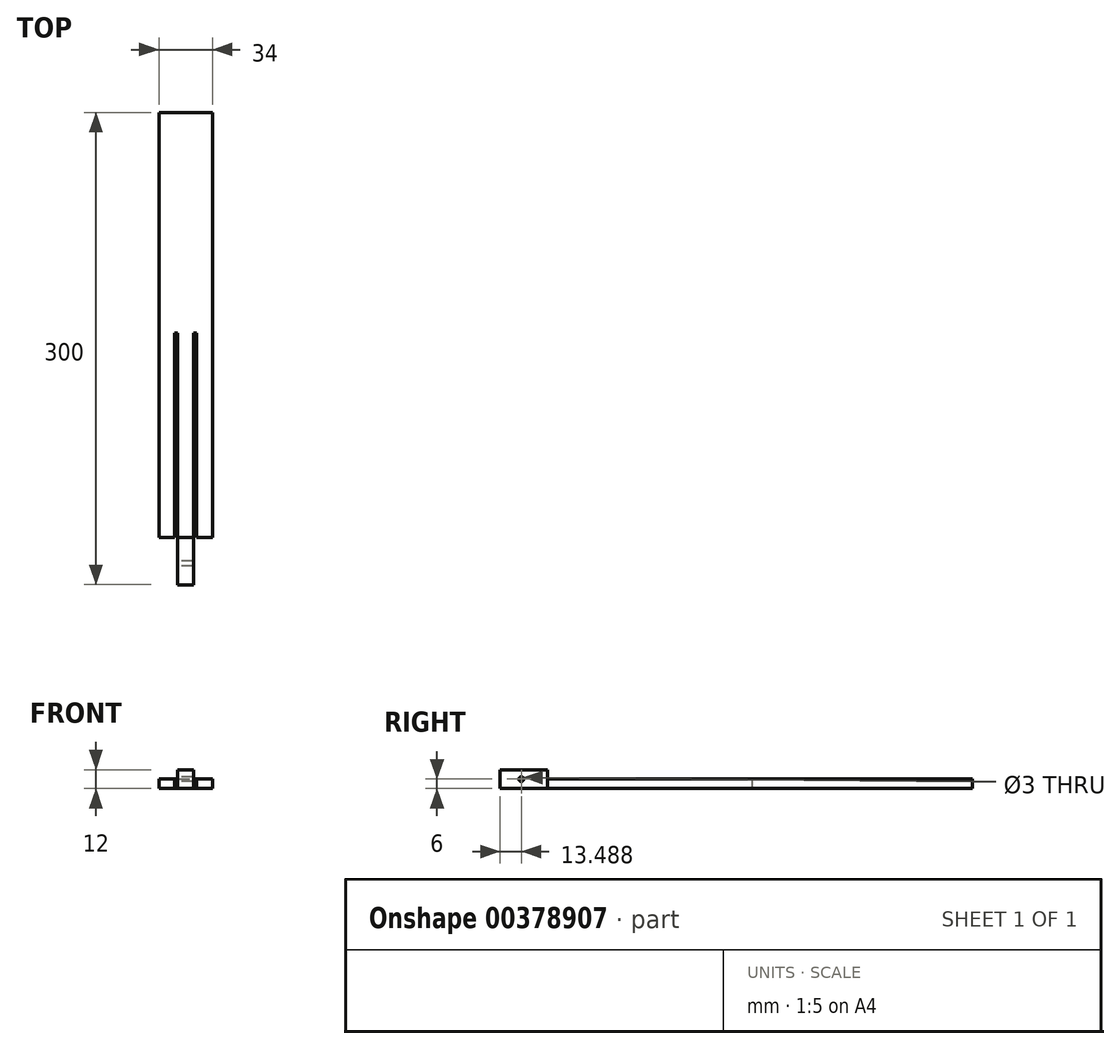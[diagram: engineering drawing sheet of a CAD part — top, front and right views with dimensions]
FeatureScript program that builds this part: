
annotation { "Feature Type Name" : "Feature", "Feature Type Description" : "" }
export const myFeature = defineFeature(function(context is Context, id is Id, definition is map)
    precondition{}
    {
        {
            var Q0;
            Q0=qCreatedBy(makeId("Top.planeOp"),FACE);
            var sketch = newSketch(context, id + "F0", { "sketchPlane" : qUnion([Q0])});
            skLineSegment(sketch, "E0.bottom", {"start": v(-19.09, 227.5) * mm, "end": v(14.91, 227.5) * mm});
            skLineSegment(sketch, "E0.left", {"start": v(-19.09, 227.5) * mm, "end": v(-19.09, -42.5) * mm});
            skLineSegment(sketch, "E0.right", {"start": v(14.91, 227.5) * mm, "end": v(14.91, -42.5) * mm});
            skLineSegment(sketch, "E1.top", {"start": v(-9.09, 87.5) * mm, "end": v(-7.09, 87.5) * mm});
            skLineSegment(sketch, "E1.left", {"start": v(-9.09, -42.5) * mm, "end": v(-9.09, 87.5) * mm});
            skLineSegment(sketch, "E1.right", {"start": v(-7.09, -72.5) * mm, "end": v(-7.09, 87.5) * mm});
            skLineSegment(sketch, "E2.top", {"start": v(2.91, 87.5) * mm, "end": v(4.91, 87.5) * mm});
            skLineSegment(sketch, "E2.left", {"start": v(2.91, -72.5) * mm, "end": v(2.91, 87.5) * mm});
            skLineSegment(sketch, "E2.right", {"start": v(4.91, -42.5) * mm, "end": v(4.91, 87.5) * mm});
            skLineSegment(sketch, "E3.trimOffspring", {"start": v(-7.09, -72.5) * mm, "end": v(2.91, -72.5) * mm});
            skLineSegment(sketch, "E4.top", {"start": v(-19.09, -42.5) * mm, "end": v(-9.09, -42.5) * mm});
            skLineSegment(sketch, "E5.top", {"start": v(4.91, -42.5) * mm, "end": v(14.91, -42.5) * mm});
            skSolve(sketch);
        }
        {
            var Q0;
            Q0=makeQuery(id+"F0.imprint","IMPRINT",FACE,{"disambiguationData":[TD([[makeQuery(id+"F0.imprint","IMPRINT",EDGE,{"derivedFrom":sQuery(id+"F0.wireOp",EDGE,"E0.bottom")}),-1.0]])]});
            extrude(context, id + "F1", {"entities" : qUnion([Q0]), "depth" : 6 * mm});
        }
        {
            var Q0;
            Q0=makeQuery(id+"F1.opExtrude","CAP_FACE",FACE,{"disambiguationData":[OSD([sQuery(id+"F0.wireOp",EDGE,"E0.bottom"),sQuery(id+"F0.wireOp",EDGE,"E0.left"),sQuery(id+"F0.wireOp",EDGE,"E0.right"),sQuery(id+"F0.wireOp",EDGE,"E1.top"),sQuery(id+"F0.wireOp",EDGE,"E1.left"),sQuery(id+"F0.wireOp",EDGE,"E1.right"),sQuery(id+"F0.wireOp",EDGE,"E2.top"),sQuery(id+"F0.wireOp",EDGE,"E2.left"),sQuery(id+"F0.wireOp",EDGE,"E2.right"),sQuery(id+"F0.wireOp",EDGE,"E3.trimOffspring"),sQuery(id+"F0.wireOp",EDGE,"E4.top"),sQuery(id+"F0.wireOp",EDGE,"E5.top")])],"isStart":false});
            var sketch = newSketch(context, id + "F2", { "sketchPlane" : qUnion([Q0])});
            skLineSegment(sketch, "E6.bottom", {"start": v(-7.09, -42.5) * mm, "end": v(2.91, -42.5) * mm});
            skLineSegment(sketch, "E6.top", {"start": v(-7.09, -72.5) * mm, "end": v(2.91, -72.5) * mm});
            skLineSegment(sketch, "E6.left", {"start": v(-7.09, -42.5) * mm, "end": v(-7.09, -72.5) * mm});
            skLineSegment(sketch, "E6.right", {"start": v(2.91, -42.5) * mm, "end": v(2.91, -72.5) * mm});
            skSolve(sketch);
        }
        {
            var Q0;
            Q0=qSketchRegion(id+"F2",true);
            extrude(context, id + "F3", {"entities" : qUnion([Q0]), "operationType" : NewBodyOperationType.ADD, "depth" : 6 * mm});
        }
        {
            var Q0;
            Q0=makeQuery(id+"F3.boolean.opBoolean","MERGE",FACE,{"derivedFrom":[makeQuery(id+"F1.opExtrude","SWEPT_FACE",FACE,{"disambiguationData":[OSD([sQuery(id+"F0.wireOp",EDGE,"E1.right")])]}),makeQuery(id+"F3.opExtrude","SWEPT_FACE",FACE,{"disambiguationData":[OSD([sQuery(id+"F2.wireOp",EDGE,"E6.left")])]})]});
            var sketch = newSketch(context, id + "F4", { "sketchPlane" : qUnion([Q0])});
            skCircle(sketch, "E7", {"center": v(59, 6) * mm, "radius": 1.5 * mm});
            skPoint(sketch, "E7.centerSnap0", {"position": v(72.5, 6) * mm});
            skSolve(sketch);
        }
        {
            var Q0;
            Q0=makeQuery(id+"F4.imprint","IMPRINT",FACE,{"disambiguationData":[TD([[makeQuery(id+"F4.imprint","IMPRINT",EDGE,{"derivedFrom":sQuery(id+"F4.wireOp",EDGE,"E7")}),1.0]])]});
            extrude(context, id + "F5", {"entities" : qUnion([Q0]), "operationType" : NewBodyOperationType.REMOVE, "endBound" : BoundingType.UP_TO_NEXT, "oppositeDirection" : true, "depth" : 25 * mm});
        }
    });
